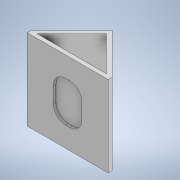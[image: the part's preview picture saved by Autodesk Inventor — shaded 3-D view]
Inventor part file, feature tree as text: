
AUTODESK INVENTOR PART (.ipt)
format: ipt  version: 2020 (Build 240168000, 168)  size: 133,632 bytes
history: native  units: mm
features: extrude x3, sketch x3
ambient origin geometry x8: Origin, YZ Plane, XZ Plane, XY Plane, X Axis, Y Axis, Z Axis, Center Point
bodies: Solid1 (feature_tree)
feature tree (6):
  extrude  "Extrusion1"  Depth=100.0mm
  extrude  "Extrusion2"  TaperAngle=45.0deg  [1 undecoded]
  extrude  "Extrusion3"  Depth=5.0mm
  sketch  "Sketch1"  dims[d0=100.0mm d1=100.0mm]
  sketch  "Sketch2"  dims[d2=5.0mm d3=0.0mm d4=45.0deg]
  sketch  "Sketch3"  dims[d5=5.0mm d6=5.0mm d7=55.0mm d8=0.0mm d9=35.0mm d10=50.0mm d11=15.0mm d12=3.0mm d13=0.0mm]
note: 1 required parameter value undecoded (feature->parameter linkage not recoverable at this tier; creation-order binding heuristic only, values carry confidence <= 0.55)
